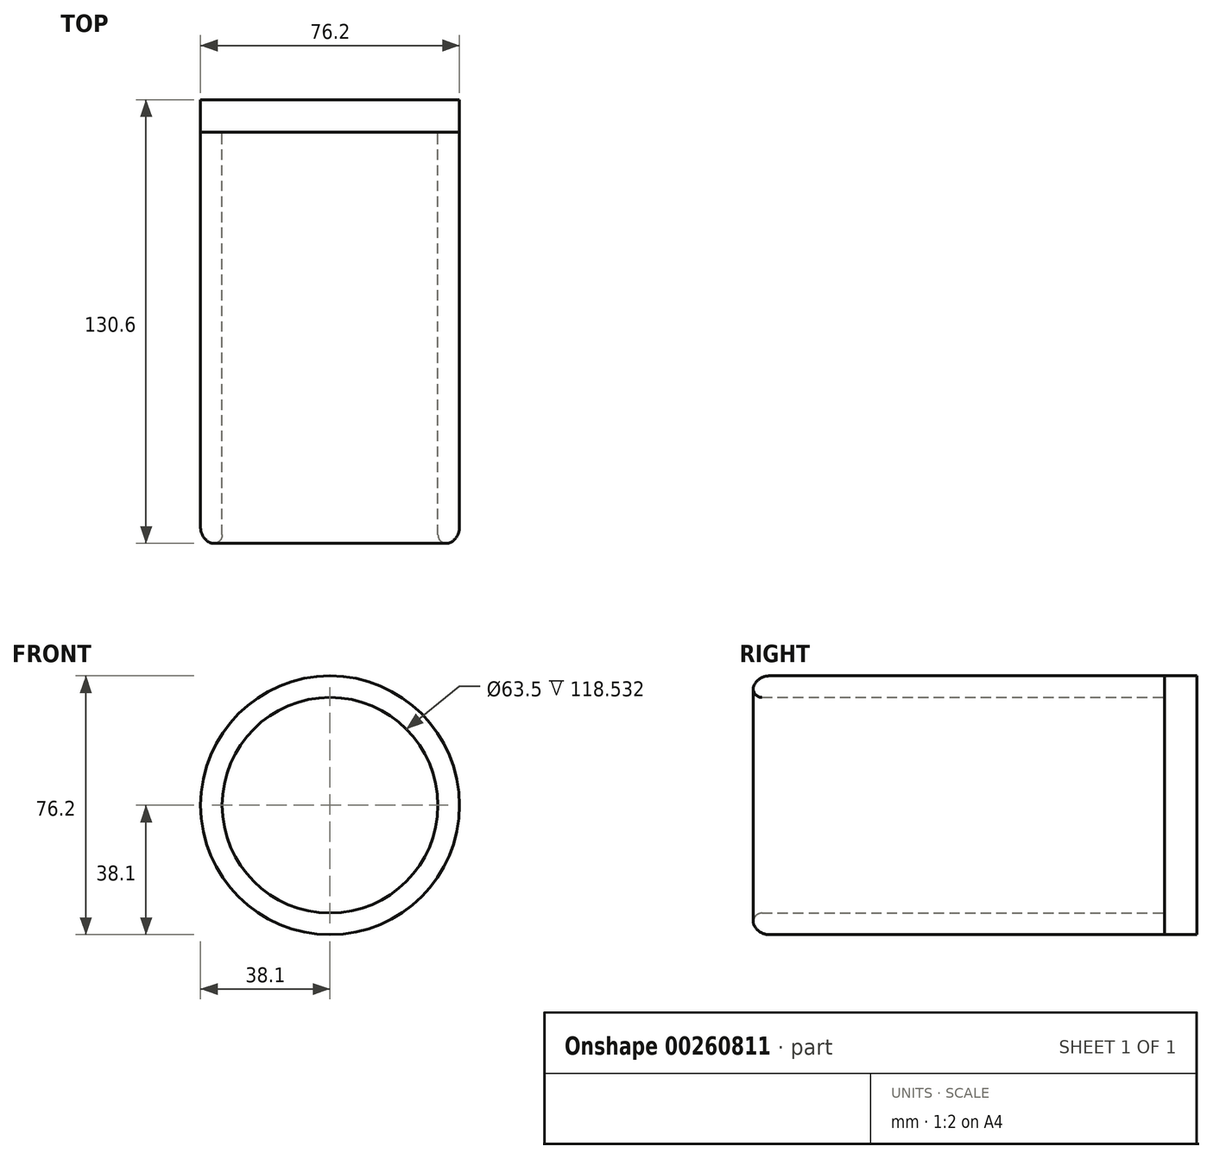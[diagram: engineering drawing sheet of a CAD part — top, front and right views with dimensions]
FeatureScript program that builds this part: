
annotation { "Feature Type Name" : "Feature", "Feature Type Description" : "" }
export const myFeature = defineFeature(function(context is Context, id is Id, definition is map)
    precondition{}
    {
        {
            var Q0;
            Q0=qCreatedBy(makeId("Front.planeOp"),FACE);
            var sketch = newSketch(context, id + "F0", { "sketchPlane" : qUnion([Q0])});
            skCircle(sketch, "E0", {"center": v(0, 0) * mm, "radius": 38.1 * mm});
            skCircle(sketch, "E1", {"center": v(0, 0) * mm, "radius": 31.75 * mm});
            skSolve(sketch);
        }
        {
            var Q0;
            Q0=makeQuery(id+"F0.imprint","IMPRINT",FACE,{"disambiguationData":[TD([[makeQuery(id+"F0.imprint","IMPRINT",EDGE,{"derivedFrom":sQuery(id+"F0.wireOp",EDGE,"E0")}),1.0]])]});
            extrude(context, id + "F1", {"entities" : qUnion([Q0]), "depth" : 121.4 * mm});
        }
        {
            var Q0;
            Q0=makeQuery(id+"F1.opExtrude","CAP_EDGE",EDGE,{"disambiguationData":[OSD([sQuery(id+"F0.wireOp",EDGE,"E0")])],"isStart":false});
            fillet(context, id + "F2", {"entities" : qUnion([Q0]), "radius" : 5.08 * mm, "tangentPropagation" : true, "allowEdgeOverflow" : false});
        }
        {
            var Q0;
            Q0=makeQuery(id+"F1.opExtrude","CAP_EDGE",EDGE,{"disambiguationData":[OSD([sQuery(id+"F0.wireOp",EDGE,"E1")])],"isStart":false});
            fillet(context, id + "F3", {"entities" : qUnion([Q0]), "radius" : 2.54 * mm, "tangentPropagation" : true, "allowEdgeOverflow" : false});
        }
        {
            var Q0;
            Q0=makeQuery(id+"F0.imprint","IMPRINT",FACE,{"disambiguationData":[TD([[makeQuery(id+"F0.imprint","IMPRINT",EDGE,{"derivedFrom":sQuery(id+"F0.wireOp",EDGE,"E0")}),1.0]])]});
            var Q1;
            Q1=makeQuery(id+"F0.imprint","IMPRINT",FACE,{"disambiguationData":[TD([[makeQuery(id+"F0.imprint","IMPRINT",EDGE,{"derivedFrom":sQuery(id+"F0.wireOp",EDGE,"E1")}),1.0]])]});
            extrude(context, id + "F4", {"entities" : qUnion([Q0, Q1]), "oppositeDirection" : true, "depth" : 9.52 * mm});
        }
    });
